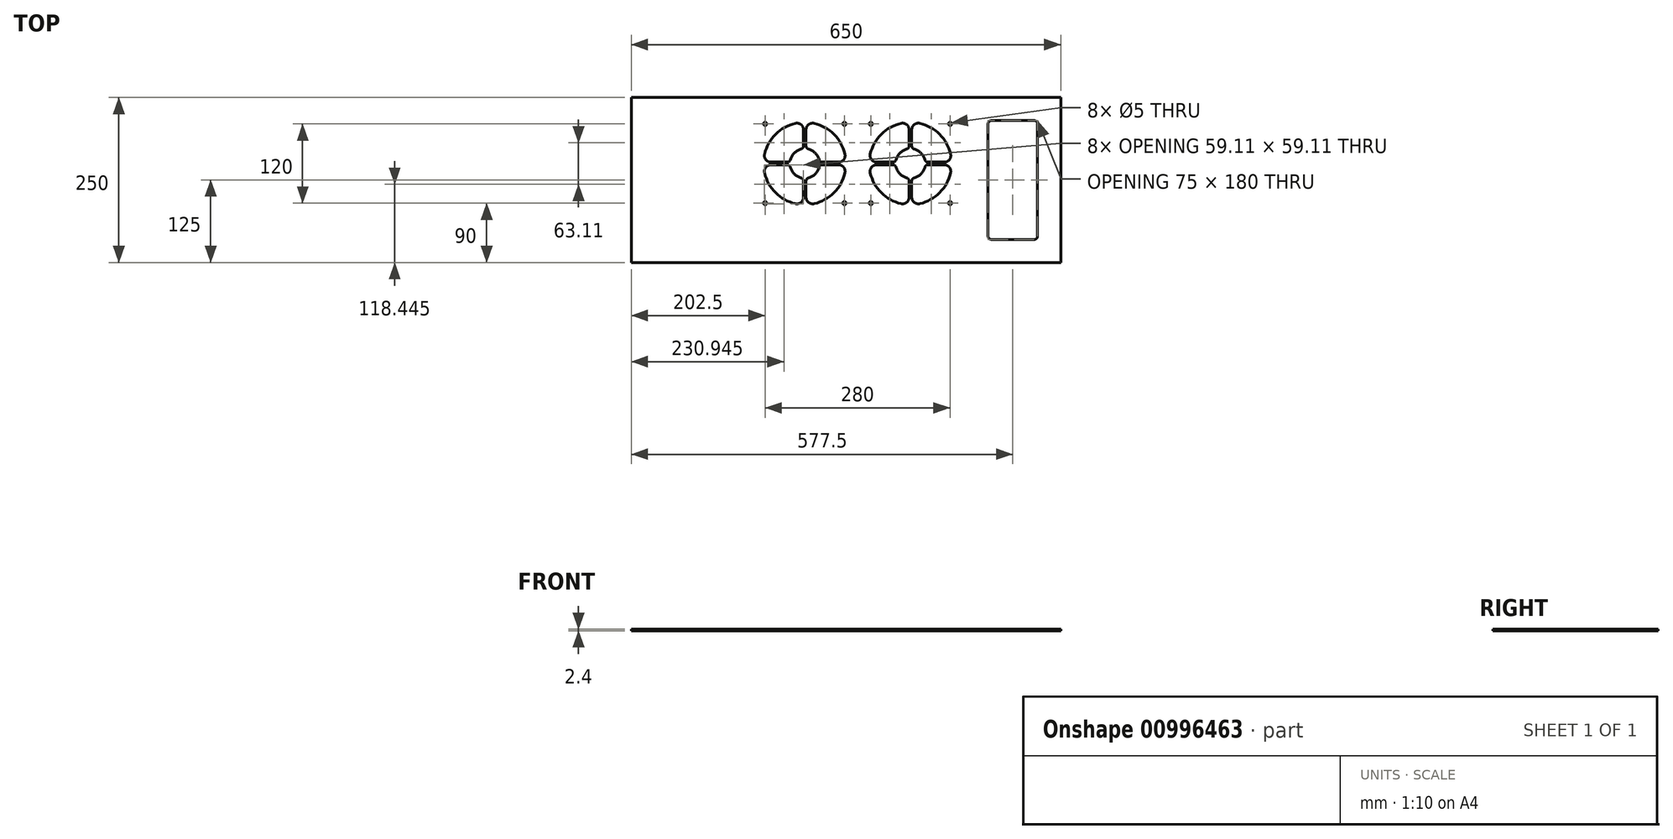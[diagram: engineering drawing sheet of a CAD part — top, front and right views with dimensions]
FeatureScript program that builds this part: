
annotation { "Feature Type Name" : "Feature", "Feature Type Description" : "" }
export const myFeature = defineFeature(function(context is Context, id is Id, definition is map)
    precondition{}
    {
        {
            var Q0;
            Q0=qCreatedBy(makeId("Top.planeOp"),FACE);
            var sketch = newSketch(context, id + "F0", { "sketchPlane" : qUnion([Q0])});
            skLineSegment(sketch, "E0.bottom", {"start": v(-325, 125) * mm, "end": v(325, 125) * mm});
            skLineSegment(sketch, "E0.top", {"start": v(-325, -125) * mm, "end": v(325, -125) * mm});
            skLineSegment(sketch, "E0.left", {"start": v(-325, 125) * mm, "end": v(-325, -125) * mm});
            skLineSegment(sketch, "E0.right", {"start": v(325, 125) * mm, "end": v(325, -125) * mm});
            skPoint(sketch, "E0.middle", {"position": v(0, 0) * mm});
            skCircle(sketch, "E1", {"center": v(-62.5, 25) * mm, "radius": 62.5 * mm});
            skCircle(sketch, "E2", {"center": v(97.5, 25) * mm, "radius": 62.5 * mm});
            skCircle(sketch, "E3", {"center": v(-62.5, 25) * mm, "radius": 22.5 * mm});
            skCircle(sketch, "E4", {"center": v(97.5, 25) * mm, "radius": 22.5 * mm});
            skLineSegment(sketch, "E5", {"start": v(-62.5, 25) * mm, "end": v(-62.5, -37.5) * mm});
            skLineSegment(sketch, "E6", {"start": v(-62.5, 25) * mm, "end": v(97.5, 25) * mm});
            skLineSegment(sketch, "E7", {"start": v(97.5, 25) * mm, "end": v(160, 25) * mm});
            skLineSegment(sketch, "E8", {"start": v(-62.5, 25) * mm, "end": v(-125, 25) * mm});
            skLineSegment(sketch, "E9", {"start": v(-62.5, 25) * mm, "end": v(-62.5, 87.5) * mm});
            skLineSegment(sketch, "E10", {"start": v(97.5, 25) * mm, "end": v(97.5, 87.5) * mm});
            skLineSegment(sketch, "E11.0", {"start": v(-64.5, 25) * mm, "end": v(-64.5, -37.5) * mm});
            skLineSegment(sketch, "E12.0", {"start": v(-60.5, 25) * mm, "end": v(-60.5, -37.5) * mm});
            skLineSegment(sketch, "E13.0", {"start": v(-62.5, 23) * mm, "end": v(97.5, 23) * mm});
            skLineSegment(sketch, "E14.0", {"start": v(-62.5, 27) * mm, "end": v(97.5, 27) * mm});
            skLineSegment(sketch, "E15.0", {"start": v(-60.5, 25) * mm, "end": v(-60.5, 87.5) * mm});
            skLineSegment(sketch, "E16.0", {"start": v(-64.5, 25) * mm, "end": v(-64.5, 87.5) * mm});
            skLineSegment(sketch, "E17.0", {"start": v(-62.5, 27) * mm, "end": v(-125, 27) * mm});
            skLineSegment(sketch, "E18.0", {"start": v(-62.5, 23) * mm, "end": v(-125, 23) * mm});
            skLineSegment(sketch, "E19.0", {"start": v(97.5, 27) * mm, "end": v(160, 27) * mm});
            skLineSegment(sketch, "E20.0", {"start": v(97.5, 23) * mm, "end": v(160, 23) * mm});
            skLineSegment(sketch, "E21.0", {"start": v(99.5, 25) * mm, "end": v(99.5, 87.5) * mm});
            skLineSegment(sketch, "E22.0", {"start": v(95.5, 25) * mm, "end": v(95.5, 87.5) * mm});
            skLineSegment(sketch, "E23", {"start": v(95.5, 25) * mm, "end": v(95.5, -37.47) * mm});
            skLineSegment(sketch, "E24", {"start": v(99.5, 25) * mm, "end": v(99.5, -37.47) * mm});
            skCircle(sketch, "E25", {"center": v(37.5, 85) * mm, "radius": 2.5 * mm});
            skCircle(sketch, "E26", {"center": v(157.5, 85) * mm, "radius": 2.5 * mm});
            skCircle(sketch, "E27", {"center": v(157.5, -35) * mm, "radius": 2.5 * mm});
            skCircle(sketch, "E28", {"center": v(37.5, -35) * mm, "radius": 2.5 * mm});
            skCircle(sketch, "E29", {"center": v(-122.5, 85) * mm, "radius": 2.5 * mm});
            skCircle(sketch, "E30", {"center": v(-2.5, 85) * mm, "radius": 2.5 * mm});
            skCircle(sketch, "E31", {"center": v(-122.5, -35) * mm, "radius": 2.5 * mm});
            skCircle(sketch, "E32", {"center": v(-2.5, -35) * mm, "radius": 2.5 * mm});
            skLineSegment(sketch, "E33.bottom", {"start": v(290, 90) * mm, "end": v(215, 90) * mm});
            skLineSegment(sketch, "E33.top", {"start": v(290, -90) * mm, "end": v(215, -90) * mm});
            skLineSegment(sketch, "E33.left", {"start": v(290, 90) * mm, "end": v(290, -90) * mm});
            skLineSegment(sketch, "E33.right", {"start": v(215, 90) * mm, "end": v(215, -90) * mm});
            skSolve(sketch);
        }
        {
            var Q0;
            Q0 = qSketchRegion(id + "F0", true);
            var Q1;
            {var subQ0=sQuery(id+"F0.wireOp",EDGE,"E16.0");var subQ1=sQuery(id+"F0.wireOp",EDGE,"E3");var subQ2=makeQuery(id+"F0.imprint","INTERSECT",VERTEX,{"derivedFrom":[subQ1,subQ0]});Q1=makeQuery(id+"F0.imprint","IMPRINT",FACE,{"disambiguationData":[TD([[makeQuery(id+"F0.imprint","IMPRINT",EDGE,{"disambiguationData":[TD([[subQ2,-1.0]])],"derivedFrom":subQ1}),1.0]])]});}
            var Q2;
            {var subQ0=sQuery(id+"F0.wireOp",EDGE,"E14.0");var subQ1=sQuery(id+"F0.wireOp",EDGE,"E3");var subQ2=makeQuery(id+"F0.imprint","INTERSECT",VERTEX,{"derivedFrom":[subQ1,subQ0]});Q2=makeQuery(id+"F0.imprint","IMPRINT",FACE,{"disambiguationData":[TD([[makeQuery(id+"F0.imprint","IMPRINT",EDGE,{"disambiguationData":[TD([[subQ2,-1.0]])],"derivedFrom":subQ1}),1.0]])]});}
            var Q3;
            {var subQ0=sQuery(id+"F0.wireOp",EDGE,"E15.0");var subQ1=sQuery(id+"F0.wireOp",EDGE,"E3");var subQ2=makeQuery(id+"F0.imprint","INTERSECT",VERTEX,{"derivedFrom":[subQ1,subQ0]});Q3=makeQuery(id+"F0.imprint","IMPRINT",FACE,{"disambiguationData":[TD([[makeQuery(id+"F0.imprint","IMPRINT",EDGE,{"disambiguationData":[TD([[subQ2,-1.0]])],"derivedFrom":subQ1}),1.0]])]});}
            var Q4;
            {var subQ0=sQuery(id+"F0.wireOp",EDGE,"E9");var subQ1=sQuery(id+"F0.wireOp",EDGE,"E3");var subQ2=makeQuery(id+"F0.imprint","INTERSECT",VERTEX,{"derivedFrom":[subQ1,subQ0]});Q4=makeQuery(id+"F0.imprint","IMPRINT",FACE,{"disambiguationData":[TD([[makeQuery(id+"F0.imprint","IMPRINT",EDGE,{"disambiguationData":[TD([[subQ2,-1.0]])],"derivedFrom":subQ1}),1.0]])]});}
            var Q5;
            {var subQ0=sQuery(id+"F0.wireOp",EDGE,"E14.0");var subQ1=sQuery(id+"F0.wireOp",EDGE,"E1");var subQ2=makeQuery(id+"F0.imprint","INTERSECT",VERTEX,{"derivedFrom":[subQ1,subQ0]});Q5=makeQuery(id+"F0.imprint","IMPRINT",FACE,{"disambiguationData":[TD([[makeQuery(id+"F0.imprint","IMPRINT",EDGE,{"disambiguationData":[TD([[subQ2,1.0]])],"derivedFrom":subQ1}),1.0]])]});}
            var Q6;
            {var subQ0=sQuery(id+"F0.wireOp",EDGE,"E6");var subQ1=sQuery(id+"F0.wireOp",EDGE,"E1");var subQ2=makeQuery(id+"F0.imprint","INTERSECT",VERTEX,{"derivedFrom":[subQ1,subQ0]});Q6=makeQuery(id+"F0.imprint","IMPRINT",FACE,{"disambiguationData":[TD([[makeQuery(id+"F0.imprint","IMPRINT",EDGE,{"disambiguationData":[TD([[subQ2,1.0]])],"derivedFrom":subQ1}),1.0]])]});}
            var Q7;
            {var subQ0=sQuery(id+"F0.wireOp",EDGE,"E14.0");var subQ1=sQuery(id+"F0.wireOp",EDGE,"E3");var subQ2=makeQuery(id+"F0.imprint","INTERSECT",VERTEX,{"derivedFrom":[subQ1,subQ0]});Q7=makeQuery(id+"F0.imprint","IMPRINT",FACE,{"disambiguationData":[TD([[makeQuery(id+"F0.imprint","IMPRINT",EDGE,{"disambiguationData":[TD([[subQ2,1.0]])],"derivedFrom":subQ1}),1.0]])]});}
            var Q8;
            {var subQ0=sQuery(id+"F0.wireOp",EDGE,"E6");var subQ1=sQuery(id+"F0.wireOp",EDGE,"E3");var subQ2=makeQuery(id+"F0.imprint","INTERSECT",VERTEX,{"derivedFrom":[subQ1,subQ0]});Q8=makeQuery(id+"F0.imprint","IMPRINT",FACE,{"disambiguationData":[TD([[makeQuery(id+"F0.imprint","IMPRINT",EDGE,{"disambiguationData":[TD([[subQ2,1.0]])],"derivedFrom":subQ1}),1.0]])]});}
            var Q9;
            {var subQ0=sQuery(id+"F0.wireOp",EDGE,"E12.0");var subQ1=sQuery(id+"F0.wireOp",EDGE,"E3");var subQ2=makeQuery(id+"F0.imprint","INTERSECT",VERTEX,{"derivedFrom":[subQ1,subQ0]});Q9=makeQuery(id+"F0.imprint","IMPRINT",FACE,{"disambiguationData":[TD([[makeQuery(id+"F0.imprint","IMPRINT",EDGE,{"disambiguationData":[TD([[subQ2,-1.0]])],"derivedFrom":subQ1}),1.0]])]});}
            var Q10;
            {var subQ0=sQuery(id+"F0.wireOp",EDGE,"E5");var subQ1=sQuery(id+"F0.wireOp",EDGE,"E3");var subQ2=makeQuery(id+"F0.imprint","INTERSECT",VERTEX,{"derivedFrom":[subQ1,subQ0]});Q10=makeQuery(id+"F0.imprint","IMPRINT",FACE,{"disambiguationData":[TD([[makeQuery(id+"F0.imprint","IMPRINT",EDGE,{"disambiguationData":[TD([[subQ2,-1.0]])],"derivedFrom":subQ1}),1.0]])]});}
            var Q11;
            {var subQ0=sQuery(id+"F0.wireOp",EDGE,"E11.0");var subQ1=sQuery(id+"F0.wireOp",EDGE,"E3");var subQ2=makeQuery(id+"F0.imprint","INTERSECT",VERTEX,{"derivedFrom":[subQ1,subQ0]});Q11=makeQuery(id+"F0.imprint","IMPRINT",FACE,{"disambiguationData":[TD([[makeQuery(id+"F0.imprint","IMPRINT",EDGE,{"disambiguationData":[TD([[subQ2,-1.0]])],"derivedFrom":subQ1}),1.0]])]});}
            var Q12;
            {var subQ3=sQuery(id+"F0.wireOp",EDGE,"E16.0");var subQ5=sQuery(id+"F0.wireOp",EDGE,"E17.0");var subQ7=makeQuery(id+"F0.imprint","INTERSECT",VERTEX,{"derivedFrom":[subQ3,subQ5]});Q12=makeQuery(id+"F0.imprint","IMPRINT",FACE,{"disambiguationData":[TD([[makeQuery(id+"F0.imprint","IMPRINT",EDGE,{"disambiguationData":[TD([[subQ7,1.0]])],"derivedFrom":subQ3}),-1.0]])]});}
            var Q13;
            {var subQ3=sQuery(id+"F0.wireOp",EDGE,"E15.0");var subQ5=sQuery(id+"F0.wireOp",EDGE,"E14.0");var subQ7=makeQuery(id+"F0.imprint","INTERSECT",VERTEX,{"derivedFrom":[subQ5,subQ3]});Q13=makeQuery(id+"F0.imprint","IMPRINT",FACE,{"disambiguationData":[TD([[makeQuery(id+"F0.imprint","IMPRINT",EDGE,{"disambiguationData":[TD([[subQ7,1.0]])],"derivedFrom":subQ5}),-1.0]])]});}
            var Q14;
            {var subQ3=sQuery(id+"F0.wireOp",EDGE,"E13.0");var subQ5=sQuery(id+"F0.wireOp",EDGE,"E12.0");var subQ7=makeQuery(id+"F0.imprint","INTERSECT",VERTEX,{"derivedFrom":[subQ5,subQ3]});Q14=makeQuery(id+"F0.imprint","IMPRINT",FACE,{"disambiguationData":[TD([[makeQuery(id+"F0.imprint","IMPRINT",EDGE,{"disambiguationData":[TD([[subQ7,1.0]])],"derivedFrom":subQ5}),-1.0]])]});}
            var Q15;
            {var subQ3=sQuery(id+"F0.wireOp",EDGE,"E18.0");var subQ5=sQuery(id+"F0.wireOp",EDGE,"E11.0");var subQ7=makeQuery(id+"F0.imprint","INTERSECT",VERTEX,{"derivedFrom":[subQ5,subQ3]});Q15=makeQuery(id+"F0.imprint","IMPRINT",FACE,{"disambiguationData":[TD([[makeQuery(id+"F0.imprint","IMPRINT",EDGE,{"disambiguationData":[TD([[subQ7,1.0]])],"derivedFrom":subQ5}),1.0]])]});}
            var Q16;
            {var subQ0=sQuery(id+"F0.wireOp",EDGE,"E8");var subQ1=sQuery(id+"F0.wireOp",EDGE,"E3");var subQ2=makeQuery(id+"F0.imprint","INTERSECT",VERTEX,{"derivedFrom":[subQ1,subQ0]});Q16=makeQuery(id+"F0.imprint","IMPRINT",FACE,{"disambiguationData":[TD([[makeQuery(id+"F0.imprint","IMPRINT",EDGE,{"disambiguationData":[TD([[subQ2,-1.0]])],"derivedFrom":subQ1}),1.0]])]});}
            var Q17;
            {var subQ0=sQuery(id+"F0.wireOp",EDGE,"E17.0");var subQ1=sQuery(id+"F0.wireOp",EDGE,"E3");var subQ2=makeQuery(id+"F0.imprint","INTERSECT",VERTEX,{"derivedFrom":[subQ1,subQ0]});Q17=makeQuery(id+"F0.imprint","IMPRINT",FACE,{"disambiguationData":[TD([[makeQuery(id+"F0.imprint","IMPRINT",EDGE,{"disambiguationData":[TD([[subQ2,-1.0]])],"derivedFrom":subQ1}),1.0]])]});}
            var Q18;
            {var subQ0=sQuery(id+"F0.wireOp",EDGE,"E18.0");var subQ1=sQuery(id+"F0.wireOp",EDGE,"E3");var subQ2=makeQuery(id+"F0.imprint","INTERSECT",VERTEX,{"derivedFrom":[subQ1,subQ0]});Q18=makeQuery(id+"F0.imprint","IMPRINT",FACE,{"disambiguationData":[TD([[makeQuery(id+"F0.imprint","IMPRINT",EDGE,{"disambiguationData":[TD([[subQ2,-1.0]])],"derivedFrom":subQ1}),1.0]])]});}
            var Q19;
            {var subQ0=sQuery(id+"F0.wireOp",EDGE,"E8");var subQ1=sQuery(id+"F0.wireOp",EDGE,"E1");var subQ2=makeQuery(id+"F0.imprint","INTERSECT",VERTEX,{"derivedFrom":[subQ1,subQ0]});Q19=makeQuery(id+"F0.imprint","IMPRINT",FACE,{"disambiguationData":[TD([[makeQuery(id+"F0.imprint","IMPRINT",EDGE,{"disambiguationData":[TD([[subQ2,-1.0]])],"derivedFrom":subQ1}),1.0]])]});}
            var Q20;
            {var subQ0=sQuery(id+"F0.wireOp",EDGE,"E8");var subQ1=sQuery(id+"F0.wireOp",EDGE,"E1");var subQ2=makeQuery(id+"F0.imprint","INTERSECT",VERTEX,{"derivedFrom":[subQ1,subQ0]});Q20=makeQuery(id+"F0.imprint","IMPRINT",FACE,{"disambiguationData":[TD([[makeQuery(id+"F0.imprint","IMPRINT",EDGE,{"disambiguationData":[TD([[subQ2,1.0]])],"derivedFrom":subQ1}),1.0]])]});}
            var Q21;
            {var subQ0=sQuery(id+"F0.wireOp",EDGE,"E9");var subQ1=sQuery(id+"F0.wireOp",EDGE,"E1");var subQ2=makeQuery(id+"F0.imprint","INTERSECT",VERTEX,{"derivedFrom":[subQ1,subQ0]});Q21=makeQuery(id+"F0.imprint","IMPRINT",FACE,{"disambiguationData":[TD([[makeQuery(id+"F0.imprint","IMPRINT",EDGE,{"disambiguationData":[TD([[subQ2,-1.0]])],"derivedFrom":subQ1}),1.0]])]});}
            var Q22;
            {var subQ0=sQuery(id+"F0.wireOp",EDGE,"E9");var subQ1=sQuery(id+"F0.wireOp",EDGE,"E1");var subQ2=makeQuery(id+"F0.imprint","INTERSECT",VERTEX,{"derivedFrom":[subQ1,subQ0]});Q22=makeQuery(id+"F0.imprint","IMPRINT",FACE,{"disambiguationData":[TD([[makeQuery(id+"F0.imprint","IMPRINT",EDGE,{"disambiguationData":[TD([[subQ2,1.0]])],"derivedFrom":subQ1}),1.0]])]});}
            var Q23;
            {var subQ0=sQuery(id+"F0.wireOp",EDGE,"E5");var subQ1=sQuery(id+"F0.wireOp",EDGE,"E1");var subQ2=makeQuery(id+"F0.imprint","INTERSECT",VERTEX,{"derivedFrom":[subQ1,subQ0]});Q23=makeQuery(id+"F0.imprint","IMPRINT",FACE,{"disambiguationData":[TD([[makeQuery(id+"F0.imprint","IMPRINT",EDGE,{"disambiguationData":[TD([[subQ2,1.0]])],"derivedFrom":subQ1}),1.0]])]});}
            var Q24;
            {var subQ0=sQuery(id+"F0.wireOp",EDGE,"E5");var subQ1=sQuery(id+"F0.wireOp",EDGE,"E1");var subQ2=makeQuery(id+"F0.imprint","INTERSECT",VERTEX,{"derivedFrom":[subQ1,subQ0]});Q24=makeQuery(id+"F0.imprint","IMPRINT",FACE,{"disambiguationData":[TD([[makeQuery(id+"F0.imprint","IMPRINT",EDGE,{"disambiguationData":[TD([[subQ2,-1.0]])],"derivedFrom":subQ1}),1.0]])]});}
            var Q25;
            {var subQ0=sQuery(id+"F0.wireOp",EDGE,"E14.0");var subQ1=sQuery(id+"F0.wireOp",EDGE,"E1");var subQ2=makeQuery(id+"F0.imprint","INTERSECT",VERTEX,{"derivedFrom":[subQ1,subQ0]});Q25=makeQuery(id+"F0.imprint","IMPRINT",FACE,{"disambiguationData":[TD([[makeQuery(id+"F0.imprint","IMPRINT",EDGE,{"disambiguationData":[TD([[subQ2,1.0]])],"derivedFrom":subQ1}),-1.0]])]});}
            var Q26;
            {var subQ0=sQuery(id+"F0.wireOp",EDGE,"E6");var subQ1=sQuery(id+"F0.wireOp",EDGE,"E1");var subQ2=makeQuery(id+"F0.imprint","INTERSECT",VERTEX,{"derivedFrom":[subQ1,subQ0]});Q26=makeQuery(id+"F0.imprint","IMPRINT",FACE,{"disambiguationData":[TD([[makeQuery(id+"F0.imprint","IMPRINT",EDGE,{"disambiguationData":[TD([[subQ2,1.0]])],"derivedFrom":subQ1}),-1.0]])]});}
            var Q27;
            {var subQ0=sQuery(id+"F0.wireOp",EDGE,"E6");var subQ1=sQuery(id+"F0.wireOp",EDGE,"E2");var subQ2=makeQuery(id+"F0.imprint","INTERSECT",VERTEX,{"derivedFrom":[subQ1,subQ0]});Q27=makeQuery(id+"F0.imprint","IMPRINT",FACE,{"disambiguationData":[TD([[makeQuery(id+"F0.imprint","IMPRINT",EDGE,{"disambiguationData":[TD([[subQ2,-1.0]])],"derivedFrom":subQ1}),1.0]])]});}
            var Q28;
            {var subQ0=sQuery(id+"F0.wireOp",EDGE,"E14.0");var subQ1=sQuery(id+"F0.wireOp",EDGE,"E2");var subQ2=makeQuery(id+"F0.imprint","INTERSECT",VERTEX,{"derivedFrom":[subQ1,subQ0]});Q28=makeQuery(id+"F0.imprint","IMPRINT",FACE,{"disambiguationData":[TD([[makeQuery(id+"F0.imprint","IMPRINT",EDGE,{"disambiguationData":[TD([[subQ2,-1.0]])],"derivedFrom":subQ1}),1.0]])]});}
            var Q29;
            {var subQ0=sQuery(id+"F0.wireOp",EDGE,"E19.0");var subQ1=sQuery(id+"F0.wireOp",EDGE,"E4");var subQ2=makeQuery(id+"F0.imprint","INTERSECT",VERTEX,{"derivedFrom":[subQ1,subQ0]});Q29=makeQuery(id+"F0.imprint","IMPRINT",FACE,{"disambiguationData":[TD([[makeQuery(id+"F0.imprint","IMPRINT",EDGE,{"disambiguationData":[TD([[subQ2,-1.0]])],"derivedFrom":subQ1}),1.0]])]});}
            var Q30;
            {var subQ0=sQuery(id+"F0.wireOp",EDGE,"E19.0");var subQ1=sQuery(id+"F0.wireOp",EDGE,"E4");var subQ2=makeQuery(id+"F0.imprint","INTERSECT",VERTEX,{"derivedFrom":[subQ1,subQ0]});Q30=makeQuery(id+"F0.imprint","IMPRINT",FACE,{"disambiguationData":[TD([[makeQuery(id+"F0.imprint","IMPRINT",EDGE,{"disambiguationData":[TD([[subQ2,1.0]])],"derivedFrom":subQ1}),1.0]])]});}
            var Q31;
            {var subQ0=sQuery(id+"F0.wireOp",EDGE,"E7");var subQ1=sQuery(id+"F0.wireOp",EDGE,"E4");var subQ2=makeQuery(id+"F0.imprint","INTERSECT",VERTEX,{"derivedFrom":[subQ1,subQ0]});Q31=makeQuery(id+"F0.imprint","IMPRINT",FACE,{"disambiguationData":[TD([[makeQuery(id+"F0.imprint","IMPRINT",EDGE,{"disambiguationData":[TD([[subQ2,1.0]])],"derivedFrom":subQ1}),1.0]])]});}
            var Q32;
            {var subQ0=sQuery(id+"F0.wireOp",EDGE,"E24");var subQ1=sQuery(id+"F0.wireOp",EDGE,"E4");var subQ2=makeQuery(id+"F0.imprint","INTERSECT",VERTEX,{"derivedFrom":[subQ1,subQ0]});Q32=makeQuery(id+"F0.imprint","IMPRINT",FACE,{"disambiguationData":[TD([[makeQuery(id+"F0.imprint","IMPRINT",EDGE,{"disambiguationData":[TD([[subQ2,-1.0]])],"derivedFrom":subQ1}),1.0]])]});}
            var Q33;
            {var subQ3=sQuery(id+"F0.wireOp",EDGE,"E23");var subQ5=sQuery(id+"F0.wireOp",EDGE,"E4");var subQ6=makeQuery(id+"F0.imprint","INTERSECT",VERTEX,{"derivedFrom":[subQ5,subQ3]});Q33=makeQuery(id+"F0.imprint","IMPRINT",FACE,{"disambiguationData":[TD([[makeQuery(id+"F0.imprint","IMPRINT",EDGE,{"disambiguationData":[TD([[subQ6,-1.0]])],"derivedFrom":subQ5}),1.0]])]});}
            var Q34;
            {var subQ0=sQuery(id+"F0.wireOp",EDGE,"E20.0");var subQ1=sQuery(id+"F0.wireOp",EDGE,"E13.0");var subQ2=makeQuery(id+"F0.imprint","INTERSECT",VERTEX,{"derivedFrom":[subQ1,subQ0]});Q34=makeQuery(id+"F0.imprint","IMPRINT",FACE,{"disambiguationData":[TD([[makeQuery(id+"F0.imprint","IMPRINT",EDGE,{"disambiguationData":[TD([[subQ2,1.0]])],"derivedFrom":subQ1}),1.0]])]});}
            var Q35;
            {var subQ3=sQuery(id+"F0.wireOp",EDGE,"E21.0");var subQ5=sQuery(id+"F0.wireOp",EDGE,"E19.0");var subQ6=makeQuery(id+"F0.imprint","INTERSECT",VERTEX,{"derivedFrom":[subQ5,subQ3]});Q35=makeQuery(id+"F0.imprint","IMPRINT",FACE,{"disambiguationData":[TD([[makeQuery(id+"F0.imprint","IMPRINT",EDGE,{"disambiguationData":[TD([[subQ6,1.0]])],"derivedFrom":subQ5}),-1.0]])]});}
            var Q36;
            {var subQ3=sQuery(id+"F0.wireOp",EDGE,"E22.0");var subQ5=sQuery(id+"F0.wireOp",EDGE,"E14.0");var subQ7=makeQuery(id+"F0.imprint","INTERSECT",VERTEX,{"derivedFrom":[subQ5,subQ3]});Q36=makeQuery(id+"F0.imprint","IMPRINT",FACE,{"disambiguationData":[TD([[makeQuery(id+"F0.imprint","IMPRINT",EDGE,{"disambiguationData":[TD([[subQ7,-1.0]])],"derivedFrom":subQ5}),-1.0]])]});}
            var Q37;
            {var subQ0=sQuery(id+"F0.wireOp",EDGE,"E10");var subQ1=sQuery(id+"F0.wireOp",EDGE,"E4");var subQ2=makeQuery(id+"F0.imprint","INTERSECT",VERTEX,{"derivedFrom":[subQ1,subQ0]});Q37=makeQuery(id+"F0.imprint","IMPRINT",FACE,{"disambiguationData":[TD([[makeQuery(id+"F0.imprint","IMPRINT",EDGE,{"disambiguationData":[TD([[subQ2,-1.0]])],"derivedFrom":subQ1}),1.0]])]});}
            var Q38;
            {var subQ0=sQuery(id+"F0.wireOp",EDGE,"E21.0");var subQ1=sQuery(id+"F0.wireOp",EDGE,"E4");var subQ2=makeQuery(id+"F0.imprint","INTERSECT",VERTEX,{"derivedFrom":[subQ1,subQ0]});Q38=makeQuery(id+"F0.imprint","IMPRINT",FACE,{"disambiguationData":[TD([[makeQuery(id+"F0.imprint","IMPRINT",EDGE,{"disambiguationData":[TD([[subQ2,-1.0]])],"derivedFrom":subQ1}),1.0]])]});}
            var Q39;
            {var subQ0=sQuery(id+"F0.wireOp",EDGE,"E22.0");var subQ1=sQuery(id+"F0.wireOp",EDGE,"E4");var subQ2=makeQuery(id+"F0.imprint","INTERSECT",VERTEX,{"derivedFrom":[subQ1,subQ0]});Q39=makeQuery(id+"F0.imprint","IMPRINT",FACE,{"disambiguationData":[TD([[makeQuery(id+"F0.imprint","IMPRINT",EDGE,{"disambiguationData":[TD([[subQ2,-1.0]])],"derivedFrom":subQ1}),1.0]])]});}
            var Q40;
            {var subQ0=sQuery(id+"F0.wireOp",EDGE,"E14.0");var subQ1=sQuery(id+"F0.wireOp",EDGE,"E4");var subQ2=makeQuery(id+"F0.imprint","INTERSECT",VERTEX,{"derivedFrom":[subQ1,subQ0]});Q40=makeQuery(id+"F0.imprint","IMPRINT",FACE,{"disambiguationData":[TD([[makeQuery(id+"F0.imprint","IMPRINT",EDGE,{"disambiguationData":[TD([[subQ2,-1.0]])],"derivedFrom":subQ1}),1.0]])]});}
            var Q41;
            {var subQ0=sQuery(id+"F0.wireOp",EDGE,"E6");var subQ1=sQuery(id+"F0.wireOp",EDGE,"E4");var subQ2=makeQuery(id+"F0.imprint","INTERSECT",VERTEX,{"derivedFrom":[subQ1,subQ0]});Q41=makeQuery(id+"F0.imprint","IMPRINT",FACE,{"disambiguationData":[TD([[makeQuery(id+"F0.imprint","IMPRINT",EDGE,{"disambiguationData":[TD([[subQ2,-1.0]])],"derivedFrom":subQ1}),1.0]])]});}
            var Q42;
            {var subQ0=sQuery(id+"F0.wireOp",EDGE,"E13.0");var subQ1=sQuery(id+"F0.wireOp",EDGE,"E4");var subQ2=makeQuery(id+"F0.imprint","INTERSECT",VERTEX,{"derivedFrom":[subQ1,subQ0]});Q42=makeQuery(id+"F0.imprint","IMPRINT",FACE,{"disambiguationData":[TD([[makeQuery(id+"F0.imprint","IMPRINT",EDGE,{"disambiguationData":[TD([[subQ2,-1.0]])],"derivedFrom":subQ1}),1.0]])]});}
            var Q43;
            {var subQ0=sQuery(id+"F0.wireOp",EDGE,"E23");var subQ1=sQuery(id+"F0.wireOp",EDGE,"E2");var subQ2=makeQuery(id+"F0.imprint","INTERSECT",VERTEX,{"derivedFrom":[subQ1,subQ0]});Q43=makeQuery(id+"F0.imprint","IMPRINT",FACE,{"disambiguationData":[TD([[makeQuery(id+"F0.imprint","IMPRINT",EDGE,{"disambiguationData":[TD([[subQ2,-1.0]])],"derivedFrom":subQ1}),1.0]])]});}
            var Q44;
            {var subQ0=sQuery(id+"F0.wireOp",EDGE,"E7");var subQ1=sQuery(id+"F0.wireOp",EDGE,"E2");var subQ2=makeQuery(id+"F0.imprint","INTERSECT",VERTEX,{"derivedFrom":[subQ1,subQ0]});Q44=makeQuery(id+"F0.imprint","IMPRINT",FACE,{"disambiguationData":[TD([[makeQuery(id+"F0.imprint","IMPRINT",EDGE,{"disambiguationData":[TD([[subQ2,1.0]])],"derivedFrom":subQ1}),1.0]])]});}
            var Q45;
            {var subQ0=sQuery(id+"F0.wireOp",EDGE,"E7");var subQ1=sQuery(id+"F0.wireOp",EDGE,"E2");var subQ2=makeQuery(id+"F0.imprint","INTERSECT",VERTEX,{"derivedFrom":[subQ1,subQ0]});Q45=makeQuery(id+"F0.imprint","IMPRINT",FACE,{"disambiguationData":[TD([[makeQuery(id+"F0.imprint","IMPRINT",EDGE,{"disambiguationData":[TD([[subQ2,-1.0]])],"derivedFrom":subQ1}),1.0]])]});}
            var Q46;
            {var subQ0=sQuery(id+"F0.wireOp",EDGE,"E10");var subQ1=sQuery(id+"F0.wireOp",EDGE,"E2");var subQ2=makeQuery(id+"F0.imprint","INTERSECT",VERTEX,{"derivedFrom":[subQ1,subQ0]});Q46=makeQuery(id+"F0.imprint","IMPRINT",FACE,{"disambiguationData":[TD([[makeQuery(id+"F0.imprint","IMPRINT",EDGE,{"disambiguationData":[TD([[subQ2,1.0]])],"derivedFrom":subQ1}),1.0]])]});}
            var Q47;
            {var subQ0=sQuery(id+"F0.wireOp",EDGE,"E10");var subQ1=sQuery(id+"F0.wireOp",EDGE,"E2");var subQ2=makeQuery(id+"F0.imprint","INTERSECT",VERTEX,{"derivedFrom":[subQ1,subQ0]});Q47=makeQuery(id+"F0.imprint","IMPRINT",FACE,{"disambiguationData":[TD([[makeQuery(id+"F0.imprint","IMPRINT",EDGE,{"disambiguationData":[TD([[subQ2,-1.0]])],"derivedFrom":subQ1}),1.0]])]});}
            extrude(context, id + "F1", {"entities" : qUnion([Q0, Q1, Q2, Q3, Q4, Q5, Q6, Q7, Q8, Q9, Q10, Q11, Q12, Q13, Q14, Q15, Q16, Q17, Q18, Q19, Q20, Q21, Q22, Q23, Q24, Q25, Q26, Q27, Q28, Q29, Q30, Q31, Q32, Q33, Q34, Q35, Q36, Q37, Q38, Q39, Q40, Q41, Q42, Q43, Q44, Q45, Q46, Q47]), "depth" : 2.4 * mm, "offsetDistance" : 25 * mm});
        }
        {
            var Q0;
            Q0=makeQuery(id+"F1.opExtrude","SWEPT_EDGE",EDGE,{"disambiguationData":[OSD([sQuery(id+"F0.wireOp",EDGE,"E3"),sQuery(id+"F0.wireOp",EDGE,"E14.0")])]});
            var Q1;
            Q1=makeQuery(id+"F1.opExtrude","SWEPT_EDGE",EDGE,{"disambiguationData":[OSD([sQuery(id+"F0.wireOp",EDGE,"E3"),sQuery(id+"F0.wireOp",EDGE,"E15.0")])]});
            var Q2;
            Q2=makeQuery(id+"F1.opExtrude","SWEPT_EDGE",EDGE,{"disambiguationData":[OSD([sQuery(id+"F0.wireOp",EDGE,"E3"),sQuery(id+"F0.wireOp",EDGE,"E16.0")])]});
            var Q3;
            Q3=makeQuery(id+"F1.opExtrude","SWEPT_EDGE",EDGE,{"disambiguationData":[OSD([sQuery(id+"F0.wireOp",EDGE,"E3"),sQuery(id+"F0.wireOp",EDGE,"E17.0")])]});
            var Q4;
            Q4=makeQuery(id+"F1.opExtrude","SWEPT_EDGE",EDGE,{"disambiguationData":[OSD([sQuery(id+"F0.wireOp",EDGE,"E3"),sQuery(id+"F0.wireOp",EDGE,"E18.0")])]});
            var Q5;
            Q5=makeQuery(id+"F1.opExtrude","SWEPT_EDGE",EDGE,{"disambiguationData":[OSD([sQuery(id+"F0.wireOp",EDGE,"E3"),sQuery(id+"F0.wireOp",EDGE,"E11.0")])]});
            var Q6;
            Q6=makeQuery(id+"F1.opExtrude","SWEPT_EDGE",EDGE,{"disambiguationData":[OSD([sQuery(id+"F0.wireOp",EDGE,"E3"),sQuery(id+"F0.wireOp",EDGE,"E12.0")])]});
            var Q7;
            Q7=makeQuery(id+"F1.opExtrude","SWEPT_EDGE",EDGE,{"disambiguationData":[OSD([sQuery(id+"F0.wireOp",EDGE,"E3"),sQuery(id+"F0.wireOp",EDGE,"E13.0")])]});
            var Q8;
            Q8=makeQuery(id+"F1.opExtrude","SWEPT_EDGE",EDGE,{"disambiguationData":[OSD([sQuery(id+"F0.wireOp",EDGE,"E4"),sQuery(id+"F0.wireOp",EDGE,"E20.0")])]});
            var Q9;
            Q9=makeQuery(id+"F1.opExtrude","SWEPT_EDGE",EDGE,{"disambiguationData":[OSD([sQuery(id+"F0.wireOp",EDGE,"E4"),sQuery(id+"F0.wireOp",EDGE,"E24")])]});
            var Q10;
            Q10=makeQuery(id+"F1.opExtrude","SWEPT_EDGE",EDGE,{"disambiguationData":[OSD([sQuery(id+"F0.wireOp",EDGE,"E4"),sQuery(id+"F0.wireOp",EDGE,"E19.0")])]});
            var Q11;
            Q11=makeQuery(id+"F1.opExtrude","SWEPT_EDGE",EDGE,{"disambiguationData":[OSD([sQuery(id+"F0.wireOp",EDGE,"E4"),sQuery(id+"F0.wireOp",EDGE,"E21.0")])]});
            var Q12;
            Q12=makeQuery(id+"F1.opExtrude","SWEPT_EDGE",EDGE,{"disambiguationData":[OSD([sQuery(id+"F0.wireOp",EDGE,"E4"),sQuery(id+"F0.wireOp",EDGE,"E22.0")])]});
            var Q13;
            Q13=makeQuery(id+"F1.opExtrude","SWEPT_EDGE",EDGE,{"disambiguationData":[OSD([sQuery(id+"F0.wireOp",EDGE,"E4"),sQuery(id+"F0.wireOp",EDGE,"E14.0")])]});
            var Q14;
            Q14=makeQuery(id+"F1.opExtrude","SWEPT_EDGE",EDGE,{"disambiguationData":[OSD([sQuery(id+"F0.wireOp",EDGE,"E4"),sQuery(id+"F0.wireOp",EDGE,"E13.0")])]});
            var Q15;
            Q15=makeQuery(id+"F1.opExtrude","SWEPT_EDGE",EDGE,{"disambiguationData":[OSD([sQuery(id+"F0.wireOp",EDGE,"E4"),sQuery(id+"F0.wireOp",EDGE,"E23")])]});
            fillet(context, id + "F2", {"entities" : qUnion([Q0, Q1, Q2, Q3, Q4, Q5, Q6, Q7, Q8, Q9, Q10, Q11, Q12, Q13, Q14, Q15]), "radius" : 5 * mm, "tangentPropagation" : true, "allowEdgeOverflow" : false});
        }
        {
            var Q0;
            Q0=makeQuery(id+"F1.opExtrude","SWEPT_EDGE",EDGE,{"disambiguationData":[OSD([sQuery(id+"F0.wireOp",EDGE,"E1"),sQuery(id+"F0.wireOp",EDGE,"E11.0")])]});
            var Q1;
            Q1=makeQuery(id+"F1.opExtrude","SWEPT_EDGE",EDGE,{"disambiguationData":[OSD([sQuery(id+"F0.wireOp",EDGE,"E1"),sQuery(id+"F0.wireOp",EDGE,"E12.0")])]});
            var Q2;
            Q2=makeQuery(id+"F1.opExtrude","SWEPT_EDGE",EDGE,{"disambiguationData":[OSD([sQuery(id+"F0.wireOp",EDGE,"E1"),sQuery(id+"F0.wireOp",EDGE,"E13.0")])]});
            var Q3;
            Q3=makeQuery(id+"F1.opExtrude","SWEPT_EDGE",EDGE,{"disambiguationData":[OSD([sQuery(id+"F0.wireOp",EDGE,"E1"),sQuery(id+"F0.wireOp",EDGE,"E14.0")])]});
            var Q4;
            Q4=makeQuery(id+"F1.opExtrude","SWEPT_EDGE",EDGE,{"disambiguationData":[OSD([sQuery(id+"F0.wireOp",EDGE,"E2"),sQuery(id+"F0.wireOp",EDGE,"E23")])]});
            var Q5;
            Q5=makeQuery(id+"F1.opExtrude","SWEPT_EDGE",EDGE,{"disambiguationData":[OSD([sQuery(id+"F0.wireOp",EDGE,"E2"),sQuery(id+"F0.wireOp",EDGE,"E24")])]});
            var Q6;
            Q6=makeQuery(id+"F1.opExtrude","SWEPT_EDGE",EDGE,{"disambiguationData":[OSD([sQuery(id+"F0.wireOp",EDGE,"E2"),sQuery(id+"F0.wireOp",EDGE,"E14.0")])]});
            var Q7;
            Q7=makeQuery(id+"F1.opExtrude","SWEPT_EDGE",EDGE,{"disambiguationData":[OSD([sQuery(id+"F0.wireOp",EDGE,"E2"),sQuery(id+"F0.wireOp",EDGE,"E13.0")])]});
            var Q8;
            Q8=makeQuery(id+"F1.opExtrude","SWEPT_EDGE",EDGE,{"disambiguationData":[OSD([sQuery(id+"F0.wireOp",EDGE,"E2"),sQuery(id+"F0.wireOp",EDGE,"E21.0")])]});
            var Q9;
            Q9=makeQuery(id+"F1.opExtrude","SWEPT_EDGE",EDGE,{"disambiguationData":[OSD([sQuery(id+"F0.wireOp",EDGE,"E1"),sQuery(id+"F0.wireOp",EDGE,"E15.0")])]});
            var Q10;
            Q10=makeQuery(id+"F1.opExtrude","SWEPT_EDGE",EDGE,{"disambiguationData":[OSD([sQuery(id+"F0.wireOp",EDGE,"E1"),sQuery(id+"F0.wireOp",EDGE,"E18.0")])]});
            var Q11;
            Q11=makeQuery(id+"F1.opExtrude","SWEPT_EDGE",EDGE,{"disambiguationData":[OSD([sQuery(id+"F0.wireOp",EDGE,"E1"),sQuery(id+"F0.wireOp",EDGE,"E17.0")])]});
            var Q12;
            Q12=makeQuery(id+"F1.opExtrude","SWEPT_EDGE",EDGE,{"disambiguationData":[OSD([sQuery(id+"F0.wireOp",EDGE,"E1"),sQuery(id+"F0.wireOp",EDGE,"E16.0")])]});
            var Q13;
            Q13=makeQuery(id+"F1.opExtrude","SWEPT_EDGE",EDGE,{"disambiguationData":[OSD([sQuery(id+"F0.wireOp",EDGE,"E2"),sQuery(id+"F0.wireOp",EDGE,"E19.0")])]});
            var Q14;
            Q14=makeQuery(id+"F1.opExtrude","SWEPT_EDGE",EDGE,{"disambiguationData":[OSD([sQuery(id+"F0.wireOp",EDGE,"E2"),sQuery(id+"F0.wireOp",EDGE,"E20.0")])]});
            var Q15;
            Q15=makeQuery(id+"F1.opExtrude","SWEPT_EDGE",EDGE,{"disambiguationData":[OSD([sQuery(id+"F0.wireOp",EDGE,"E2"),sQuery(id+"F0.wireOp",EDGE,"E22.0")])]});
            fillet(context, id + "F3", {"entities" : qUnion([Q0, Q1, Q2, Q3, Q4, Q5, Q6, Q7, Q8, Q9, Q10, Q11, Q12, Q13, Q14, Q15]), "radius" : 10 * mm, "tangentPropagation" : true, "allowEdgeOverflow" : false});
        }
        {
            var Q0;
            Q0=makeQuery(id+"F1.opExtrude","SWEPT_EDGE",EDGE,{"disambiguationData":[OSD([sQuery(id+"F0.wireOp",EDGE,"E33.bottom"),sQuery(id+"F0.wireOp",EDGE,"E33.right")])]});
            var Q1;
            Q1=makeQuery(id+"F1.opExtrude","SWEPT_EDGE",EDGE,{"disambiguationData":[OSD([sQuery(id+"F0.wireOp",EDGE,"E33.bottom"),sQuery(id+"F0.wireOp",EDGE,"E33.left")])]});
            var Q2;
            Q2=makeQuery(id+"F1.opExtrude","SWEPT_EDGE",EDGE,{"disambiguationData":[OSD([sQuery(id+"F0.wireOp",EDGE,"E33.top"),sQuery(id+"F0.wireOp",EDGE,"E33.right")])]});
            var Q3;
            Q3=makeQuery(id+"F1.opExtrude","SWEPT_EDGE",EDGE,{"disambiguationData":[OSD([sQuery(id+"F0.wireOp",EDGE,"E33.top"),sQuery(id+"F0.wireOp",EDGE,"E33.left")])]});
            fillet(context, id + "F4", {"entities" : qUnion([Q0, Q1, Q2, Q3]), "radius" : 5 * mm, "tangentPropagation" : true, "allowEdgeOverflow" : false});
        }
    });
